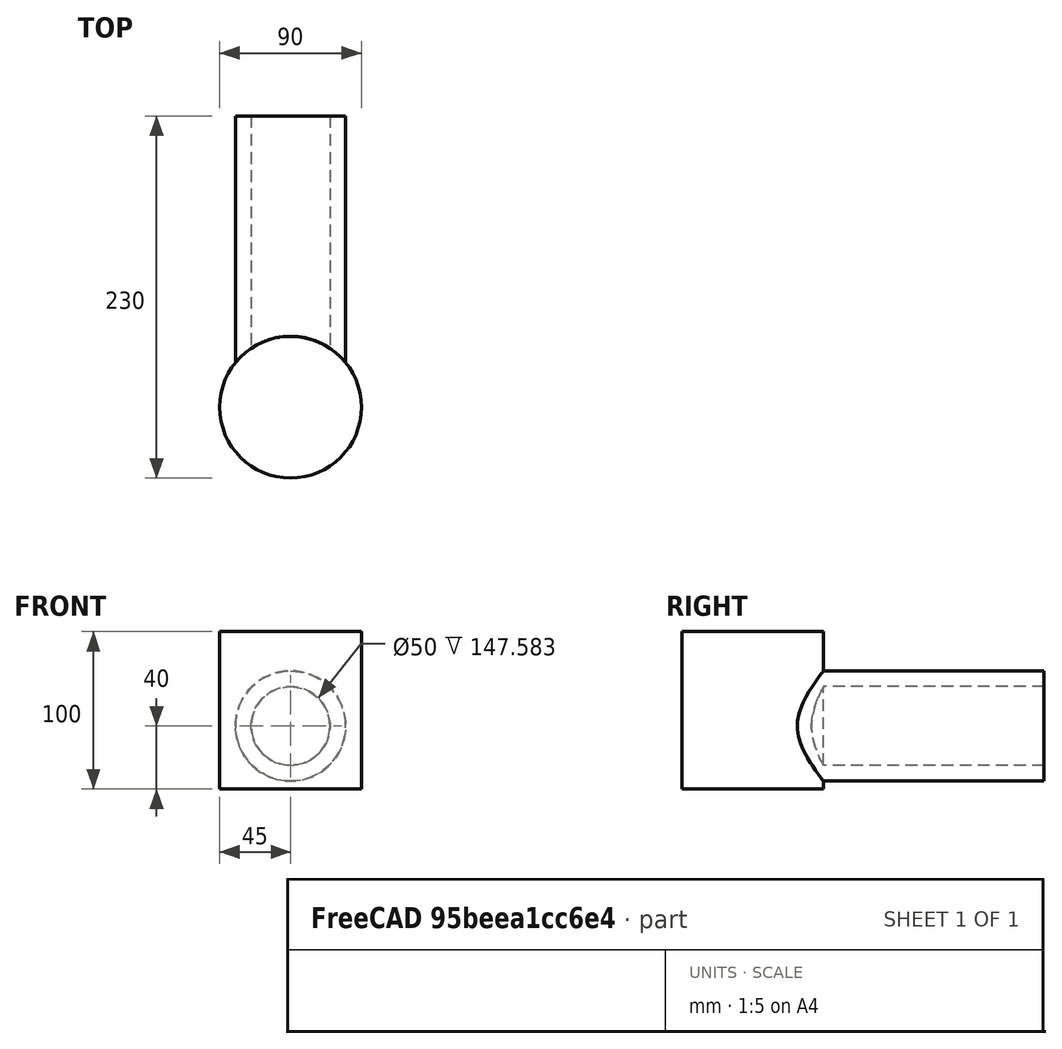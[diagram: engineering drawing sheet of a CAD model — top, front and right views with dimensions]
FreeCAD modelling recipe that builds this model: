
FCSTD DOCUMENT  (FreeCAD 0.19R24366 (Git))
Label: link_3
License: All rights reserved
LicenseURL: http://en.wikipedia.org/wiki/All_rights_reserved
objects: Sketcher::SketchObject×3, PartDesign::Pad×2, PartDesign::Revolution×1, PartDesign::Point×1, PartDesign::Body×1, Mesh::Feature×1
note: 11 computed .brp shape members not serialized (recipe doc carries the construction recipe); baked Part::Feature solids carry a one-line shape summary decoded from their .brp

FEATURE [Sketcher::SketchObject] Sketch
  FullyConstrained = true
  MapMode = 5
  Support = -> [XY_Plane]
  sketch-geometry (4):
    g0: LineSegment StartX=0 StartY=35 StartZ=0 EndX=185 EndY=35 EndZ=0
    g1: LineSegment StartX=185 StartY=35 StartZ=0 EndX=185 EndY=25 EndZ=0
    g2: LineSegment StartX=185 StartY=25 StartZ=0 EndX=0 EndY=25 EndZ=0
    g3: LineSegment StartX=0 StartY=25 StartZ=0 EndX=0 EndY=35 EndZ=0
  constraints (12):
    c: Coincident(g0,g1)
    c: Coincident(g1,g2)
    c: Coincident(g2,g3)
    c: Coincident(g3,g0)
    c: Horizontal(g0)
    c: Horizontal(g2)
    c: Vertical(g1)
    c: Vertical(g3)
    c: PointOnObject(g0,g-2)
    c: DistanceX(g0,g0) = 185
    c: DistanceY(g1,g1) = 10
    c: DistanceY(g-1,g0) = 35
FEATURE [PartDesign::Revolution] Revolution
  Angle = 360
  Axis = (1,0,0)
  Base = (0,0,0)
  Profile = -> Sketch
  ReferenceAxis = -> X_Axis
FEATURE [Sketcher::SketchObject] Sketch001
  FullyConstrained = true
  MapMode = 5
  Support = -> [XY_Plane]
  sketch-geometry (1):
    g0: Circle CenterX=0 CenterY=0 CenterZ=0 NormalX=0 NormalY=0 NormalZ=1 AngleXU=0 Radius=45
  constraints (2):
    c: Coincident(g0,g-1)
    c: Diameter(g0) = 90
FEATURE [PartDesign::Pad] Pad
  BaseFeature = -> Revolution
  Direction = (1,1,1)
  Length = 80
  Length2 = 100
  Midplane = true
  Profile = -> Sketch001
  Type = 0
FEATURE [Sketcher::SketchObject] Sketch002
  ExternalGeometry = -> [Pad]
  FullyConstrained = true
  MapMode = 5
  Placement = pos=(0,0,40) rot=(0,0,1;0rad)
  Support = -> [Pad]
  sketch-geometry (1):
    g0: Circle CenterX=0 CenterY=0 CenterZ=0 NormalX=0 NormalY=0 NormalZ=1 AngleXU=0 Radius=45
  constraints (2):
    c: Coincident(g0,g-1)
    c: Equal(g0,g-3)
FEATURE [PartDesign::Pad] Pad001
  BaseFeature = -> Pad
  Direction = (1,1,1)
  Length = 20
  Length2 = 100
  Profile = -> Sketch002
  Type = 0
FEATURE [PartDesign::Point] DatumPoint
  AttacherType = Attacher::AttachEnginePoint
  MapMode = 36
  Placement = pos=(0,0,-40) rot=(1,0,0;1.5708rad)
  Support = -> [Pad001]
FEATURE [PartDesign::Body] Body
  Group = -> [Sketch,Revolution,Sketch001,Pad,Sketch002,Pad001,DatumPoint]
  Origin = -> Origin
  Placement = pos=(0,0,-60) rot=(0,0,1;1.5708rad)
  Tip = -> Pad001
FEATURE [Mesh::Feature] Mesh  label="Body (Meshed)"
